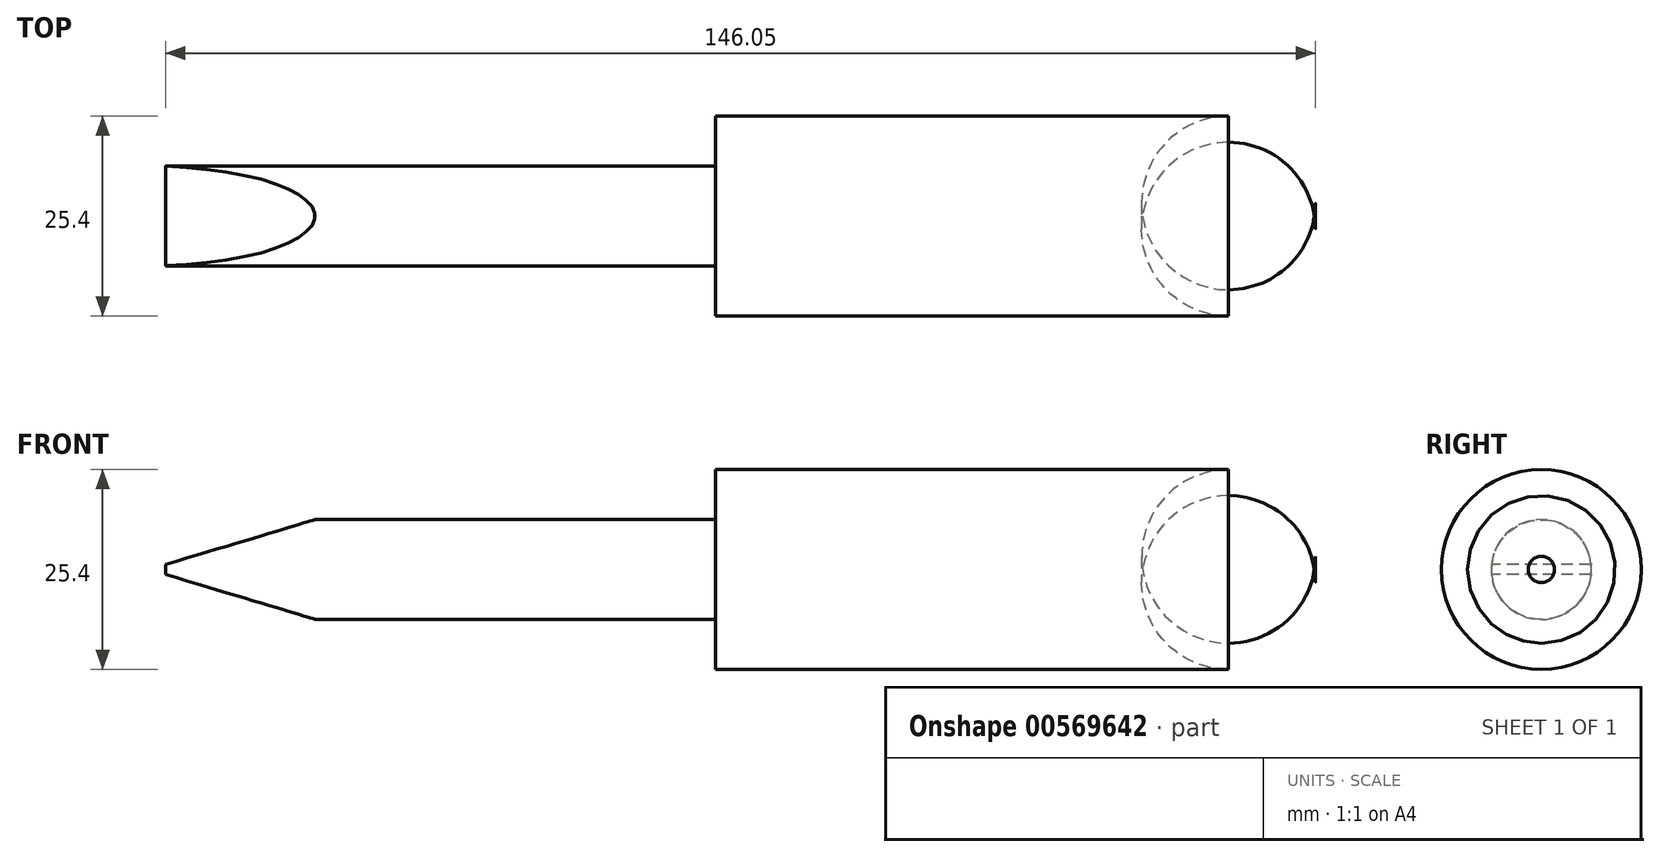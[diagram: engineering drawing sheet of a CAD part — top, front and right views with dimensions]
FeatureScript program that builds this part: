
annotation { "Feature Type Name" : "Feature", "Feature Type Description" : "" }
export const myFeature = defineFeature(function(context is Context, id is Id, definition is map)
    precondition{}
    {
        {
            var Q0;
            Q0=qCreatedBy(makeId("Front.planeOp"),FACE);
            var sketch = newSketch(context, id + "F0", { "sketchPlane" : qUnion([Q0])});
            skLineSegment(sketch, "E0.bottom", {"start": v(0, 12.7) * mm, "end": v(76.2, 12.7) * mm});
            skLineSegment(sketch, "E0.top", {"start": v(0, -12.7) * mm, "end": v(76.2, -12.7) * mm});
            skLineSegment(sketch, "E0.left", {"start": v(0, 12.7) * mm, "end": v(0, -12.7) * mm});
            skLineSegment(sketch, "E0.right", {"start": v(76.2, 12.7) * mm, "end": v(76.2, -12.7) * mm});
            skPoint(sketch, "E0.middle", {"position": v(38.1, 0) * mm});
            skLineSegment(sketch, "E1.bottom", {"start": v(0, 6.35) * mm, "end": v(-50.8, 6.35) * mm});
            skLineSegment(sketch, "E1.top", {"start": v(0, -6.35) * mm, "end": v(-50.8, -6.35) * mm});
            skLineSegment(sketch, "E1.left", {"start": v(0, 6.35) * mm, "end": v(0, -6.35) * mm});
            skLineSegment(sketch, "E1.right", {"start": v(-50.8, 6.35) * mm, "end": v(-50.8, -6.35) * mm});
            skPoint(sketch, "E1.middle", {"position": v(-25.4, 0) * mm});
            skLineSegment(sketch, "E2.bottom", {"start": v(-50.8, 0.63) * mm, "end": v(-69.85, 0.63) * mm});
            skLineSegment(sketch, "E2.top", {"start": v(-50.8, -0.64) * mm, "end": v(-69.85, -0.64) * mm});
            skLineSegment(sketch, "E2.left", {"start": v(-50.8, 0.63) * mm, "end": v(-50.8, -0.64) * mm});
            skLineSegment(sketch, "E2.right", {"start": v(-69.85, 0.63) * mm, "end": v(-69.85, -0.64) * mm});
            skPoint(sketch, "E2.middle", {"position": v(-60.33, 0) * mm});
            skLineSegment(sketch, "E3", {"start": v(-50.8, 6.35) * mm, "end": v(-69.85, 0.63) * mm});
            skLineSegment(sketch, "E4", {"start": v(-69.85, -0.64) * mm, "end": v(-50.8, -6.35) * mm});
            skLineSegment(sketch, "E5", {"start": v(76.2, 0) * mm, "end": v(-69.85, 0) * mm});
            skLineSegment(sketch, "E6.bottom", {"start": v(-50.8, -6.35) * mm, "end": v(-69.85, -6.35) * mm});
            skLineSegment(sketch, "E6.top", {"start": v(-50.8, 6.35) * mm, "end": v(-69.85, 6.35) * mm});
            skLineSegment(sketch, "E6.left", {"start": v(-50.8, -6.35) * mm, "end": v(-50.8, 6.35) * mm});
            skLineSegment(sketch, "E6.right", {"start": v(-69.85, -6.35) * mm, "end": v(-69.85, 6.35) * mm});
            skSolve(sketch);
        }
        {
            var Q0;
            {var subQ5=sQuery(id+"F0.wireOp",EDGE,"E1.bottom");Q0=makeQuery(id+"F0.imprint","IMPRINT",FACE,{"disambiguationData":[TD([[makeQuery(id+"F0.imprint","IMPRINT",EDGE,{"derivedFrom":subQ5}),1.0]])]});}
            var Q1;
            {var subQ6=sQuery(id+"F0.wireOp",EDGE,"E0.bottom");Q1=makeQuery(id+"F0.imprint","IMPRINT",FACE,{"disambiguationData":[TD([[makeQuery(id+"F0.imprint","IMPRINT",EDGE,{"derivedFrom":subQ6}),-1.0]])]});}
            var Q2;
            {var subQ2=sQuery(id+"F0.wireOp",EDGE,"E2.bottom");Q2=makeQuery(id+"F0.imprint","IMPRINT",FACE,{"disambiguationData":[TD([[makeQuery(id+"F0.imprint","IMPRINT",EDGE,{"derivedFrom":subQ2}),-1.0]])]});}
            var Q3;
            {var subQ0=sQuery(id+"F0.wireOp",EDGE,"E2.bottom");Q3=makeQuery(id+"F0.imprint","IMPRINT",FACE,{"disambiguationData":[TD([[makeQuery(id+"F0.imprint","IMPRINT",EDGE,{"derivedFrom":subQ0}),1.0]])]});}
            var Q4;
            {var subQ0=sQuery(id+"F0.wireOp",EDGE,"E3");Q4=makeQuery(id+"F0.imprint","IMPRINT",FACE,{"disambiguationData":[TD([[makeQuery(id+"F0.imprint","IMPRINT",EDGE,{"derivedFrom":subQ0}),-1.0]])]});}
            var Q5;
            Q5=sQuery(id+"F0.wireOp",EDGE,"E5");
            revolve(context, id + "F1", {"entities" : qUnion([Q0, Q1, Q2, Q3, Q4]), "axis" : qUnion([Q5]), "revolveType" : RevolveType.FULL});
        }
        {
            var Q0;
            {var subQ0=sQuery(id+"F0.wireOp",EDGE,"E3");Q0=makeQuery(id+"F0.imprint","IMPRINT",FACE,{"disambiguationData":[TD([[makeQuery(id+"F0.imprint","IMPRINT",EDGE,{"derivedFrom":subQ0}),-1.0]])]});}
            var Q1;
            {var subQ0=sQuery(id+"F0.wireOp",EDGE,"E4");Q1=makeQuery(id+"F0.imprint","IMPRINT",FACE,{"disambiguationData":[TD([[makeQuery(id+"F0.imprint","IMPRINT",EDGE,{"derivedFrom":subQ0}),-1.0]])]});}
            var Q2;
            Q2=makeQuery(id+"F1.opRevolve","SWEPT_FACE",FACE,{"disambiguationData":[OSD([sQuery(id+"F0.wireOp",EDGE,"E6.top")])]});
            extrude(context, id + "F2", {"entities" : qUnion([Q0, Q1]), "operationType" : NewBodyOperationType.REMOVE, "endBound" : BoundingType.SYMMETRIC, "oppositeDirection" : true, "depth" : 25.4 * mm, "endBoundEntityFace" : qUnion([Q2]), "offsetDistance" : 25.4 * mm});
        }
        {
            var Q0;
            Q0=makeQuery(id+"F1.opRevolve","SWEPT_EDGE",EDGE,{"disambiguationData":[OSD([sQuery(id+"F0.wireOp",EDGE,"E0.bottom"),sQuery(id+"F0.wireOp",EDGE,"E0.right")])]});
            fillet(context, id + "F3", {"entities" : qUnion([Q0]), "radius" : 11.04 * mm, "tangentPropagation" : true, "allowEdgeOverflow" : false});
        }
    });
